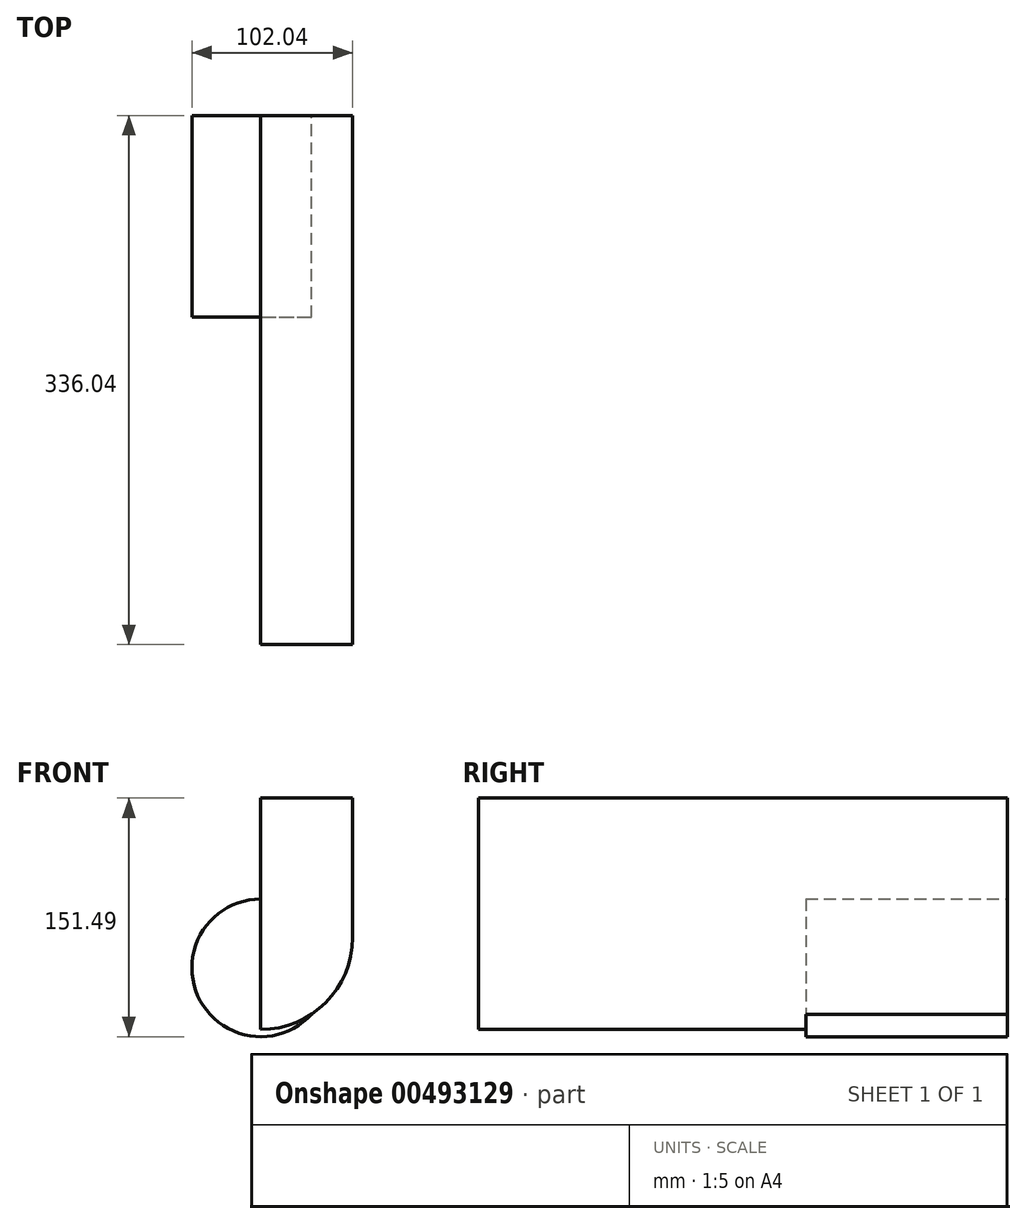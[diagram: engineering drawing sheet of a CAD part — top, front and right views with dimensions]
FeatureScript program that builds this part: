
annotation { "Feature Type Name" : "Feature", "Feature Type Description" : "" }
export const myFeature = defineFeature(function(context is Context, id is Id, definition is map)
    precondition{}
    {
        {
            var Q0;
            Q0=qCreatedBy(makeId("Front.planeOp"),FACE);
            var sketch = newSketch(context, id + "F0", { "sketchPlane" : qUnion([Q0])});
            skLineSegment(sketch, "E0.bottom", {"start": v(0, 0) * mm, "end": v(-36.53, 0) * mm});
            skLineSegment(sketch, "E0.top", {"start": v(0, 20.9) * mm, "end": v(-36.53, 20.9) * mm});
            skLineSegment(sketch, "E0.left", {"start": v(0, 0) * mm, "end": v(0, 20.9) * mm});
            skLineSegment(sketch, "E0.right", {"start": v(-36.53, 0) * mm, "end": v(-36.53, 20.9) * mm});
            skLineSegment(sketch, "E1.bottom", {"start": v(0, 0) * mm, "end": v(68.52, 0) * mm});
            skLineSegment(sketch, "E1.top", {"start": v(0, -63.48) * mm, "end": v(68.52, -63.48) * mm});
            skLineSegment(sketch, "E1.left", {"start": v(0, 0) * mm, "end": v(0, -63.48) * mm});
            skLineSegment(sketch, "E1.right", {"start": v(68.52, 0) * mm, "end": v(68.52, -63.48) * mm});
            skCircle(sketch, "E2", {"center": v(0, 0) * mm, "radius": 58.32 * mm});
            skSolve(sketch);
        }
        {
            var Q0;
            Q0=qCreatedBy(makeId("Front.planeOp"),FACE);
            var sketch = newSketch(context, id + "F1", { "sketchPlane" : qUnion([Q0])});
            skCircle(sketch, "E3", {"center": v(0, -19.13) * mm, "radius": 43.72 * mm});
            skSolve(sketch);
        }
        {
            var Q0;
            {var subQ1=sQuery(id+"F0.wireOp",EDGE,"E1.bottom");var subQ3=sQuery(id+"F0.wireOp",EDGE,"E2");var subQ4=makeQuery(id+"F0.imprint","INTERSECT",VERTEX,{"derivedFrom":[subQ1,subQ3]});Q0=makeQuery(id+"F0.imprint","IMPRINT",FACE,{"disambiguationData":[TD([[makeQuery(id+"F0.imprint","IMPRINT",EDGE,{"disambiguationData":[TD([[subQ4,1.0]])],"derivedFrom":subQ3}),1.0]])]});}
            extrude(context, id + "F2", {"entities" : qUnion([Q0]), "depth" : 25.4 * mm});
        }
        {
            var Q0;
            Q0=makeQuery(id+"F2.opExtrude","SWEPT_FACE",FACE,{"disambiguationData":[OSD([sQuery(id+"F0.wireOp",EDGE,"E1.bottom")])]});
            extrude(context, id + "F3", {"entities" : qUnion([Q0]), "operationType" : NewBodyOperationType.ADD, "depth" : 88.65 * mm});
        }
        {
            var Q0;
            {var subQ0=sQuery(id+"F0.wireOp",EDGE,"E1.bottom");Q0=makeQuery(id+"F3.boolean.opBoolean","MERGE",FACE,{"derivedFrom":[makeQuery(id+"F2.opExtrude","CAP_FACE",FACE,{"disambiguationData":[OSD([subQ0,sQuery(id+"F0.wireOp",EDGE,"E1.left"),sQuery(id+"F0.wireOp",EDGE,"E2")])],"isStart":false}),makeQuery(id+"F3.opExtrude","SWEPT_FACE",FACE,{"disambiguationData":[OSD([subQ0]),TDD([makeQuery(id+"F2.opExtrude","CAP_EDGE",EDGE,{"disambiguationData":[OSD([subQ0])],"isStart":false})])]})]});}
            extrude(context, id + "F4", {"entities" : qUnion([Q0]), "operationType" : NewBodyOperationType.ADD, "depth" : 310.64 * mm});
        }
        {
            var Q0;
            Q0=makeQuery(id+"F1.imprint","IMPRINT",FACE,{"disambiguationData":[TD([[makeQuery(id+"F1.imprint","IMPRINT",EDGE,{"derivedFrom":sQuery(id+"F1.wireOp",EDGE,"E3")}),1.0]])]});
            extrude(context, id + "F5", {"entities" : qUnion([Q0]), "operationType" : NewBodyOperationType.ADD, "depth" : 128.02 * mm});
        }
    });
